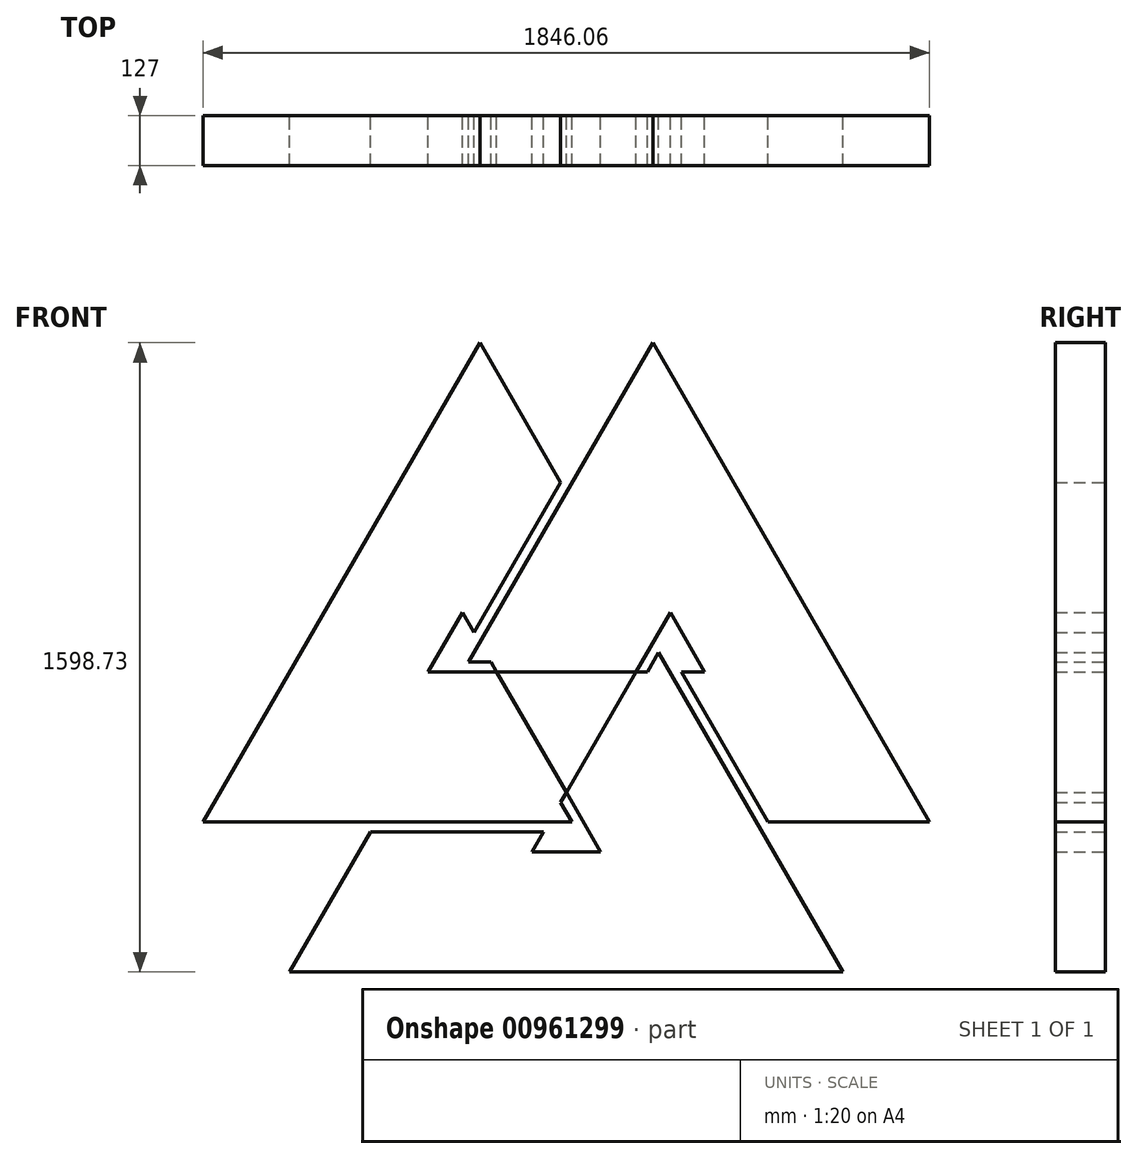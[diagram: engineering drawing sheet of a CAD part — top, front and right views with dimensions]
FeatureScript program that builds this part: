
annotation { "Feature Type Name" : "Feature", "Feature Type Description" : "" }
export const myFeature = defineFeature(function(context is Context, id is Id, definition is map)
    precondition{}
    {
        {
            var Q0;
            Q0=qCreatedBy(makeId("Front.planeOp"),FACE);
            var sketch = newSketch(context, id + "F0", { "sketchPlane" : qUnion([Q0])});
            skLineSegment(sketch, "E0", {"start": v(0, 0) * mm, "end": v(2286, 0) * mm});
            skLineSegment(sketch, "E1", {"start": v(2286, 0) * mm, "end": v(1143, 1979.73) * mm});
            skLineSegment(sketch, "E2", {"start": v(1143, 1979.73) * mm, "end": v(0, 0) * mm});
            skLineSegment(sketch, "E3", {"start": v(2346.83, 304.8) * mm, "end": v(-509.39, 304.8) * mm});
            skLineSegment(sketch, "E4", {"start": v(-334.16, 355.6) * mm, "end": v(2298.64, 355.6) * mm});
            skLineSegment(sketch, "E5", {"start": v(2223.65, 381) * mm, "end": v(-198.36, 381) * mm});
            skLineSegment(sketch, "E6", {"start": v(-45.03, 762) * mm, "end": v(2119.03, 762) * mm});
            skLineSegment(sketch, "E7", {"start": v(1921.9, 787.4) * mm, "end": v(200.29, 787.4) * mm});
            skLineSegment(sketch, "E8", {"start": v(2071.19, -237.53) * mm, "end": v(818.25, 1932.62) * mm});
            skLineSegment(sketch, "E9", {"start": v(806.35, 1851.63) * mm, "end": v(1965.85, -156.68) * mm});
            skLineSegment(sketch, "E10", {"start": v(1881.83, -61.95) * mm, "end": v(724.51, 1942.57) * mm});
            skLineSegment(sketch, "E11", {"start": v(1430.6, 1868.27) * mm, "end": v(168.06, -318.51) * mm});
            skLineSegment(sketch, "E12", {"start": v(281.56, -223.53) * mm, "end": v(1464.91, 1826.1) * mm});
            skLineSegment(sketch, "E13", {"start": v(1447.2, 1744.6) * mm, "end": v(340.04, -173.03) * mm});
            skLineSegment(sketch, "E14", {"start": v(1524.57, -255.97) * mm, "end": v(417.23, 1662) * mm});
            skLineSegment(sketch, "E15", {"start": v(472.91, 1616.36) * mm, "end": v(1604.16, -343.02) * mm});
            skLineSegment(sketch, "E16", {"start": v(715, -285.6) * mm, "end": v(1720.82, 1456.54) * mm});
            skLineSegment(sketch, "E17", {"start": v(1650.04, 1283.16) * mm, "end": v(696.9, -367.74) * mm});
            skSolve(sketch);
        }
        {
            var Q0;
            {var subQ0=sQuery(id+"F0.wireOp",EDGE,"E13");var subQ1=sQuery(id+"F0.wireOp",EDGE,"E0");var subQ2=makeQuery(id+"F0.imprint","INTERSECT",VERTEX,{"derivedFrom":[subQ1,subQ0]});Q0=makeQuery(id+"F0.imprint","IMPRINT",FACE,{"disambiguationData":[TD([[makeQuery(id+"F0.imprint","IMPRINT",EDGE,{"disambiguationData":[TD([[subQ2,-1.0]])],"derivedFrom":subQ1}),1.0]])]});}
            var Q1;
            {var subQ0=sQuery(id+"F0.wireOp",EDGE,"E16");var subQ1=sQuery(id+"F0.wireOp",EDGE,"E3");var subQ2=makeQuery(id+"F0.imprint","INTERSECT",VERTEX,{"derivedFrom":[subQ1,subQ0]});Q1=makeQuery(id+"F0.imprint","IMPRINT",FACE,{"disambiguationData":[TD([[makeQuery(id+"F0.imprint","IMPRINT",EDGE,{"disambiguationData":[TD([[subQ2,-1.0]])],"derivedFrom":subQ1}),-1.0]])]});}
            var Q2;
            {var subQ0=sQuery(id+"F0.wireOp",EDGE,"E16");var subQ1=sQuery(id+"F0.wireOp",EDGE,"E0");var subQ2=makeQuery(id+"F0.imprint","INTERSECT",VERTEX,{"derivedFrom":[subQ1,subQ0]});Q2=makeQuery(id+"F0.imprint","IMPRINT",FACE,{"disambiguationData":[TD([[makeQuery(id+"F0.imprint","IMPRINT",EDGE,{"disambiguationData":[TD([[subQ2,-1.0]])],"derivedFrom":subQ1}),1.0]])]});}
            var Q3;
            {var subQ0=sQuery(id+"F0.wireOp",EDGE,"E14");var subQ1=sQuery(id+"F0.wireOp",EDGE,"E0");var subQ2=makeQuery(id+"F0.imprint","INTERSECT",VERTEX,{"derivedFrom":[subQ1,subQ0]});Q3=makeQuery(id+"F0.imprint","IMPRINT",FACE,{"disambiguationData":[TD([[makeQuery(id+"F0.imprint","IMPRINT",EDGE,{"disambiguationData":[TD([[subQ2,-1.0]])],"derivedFrom":subQ1}),1.0]])]});}
            var Q4;
            {var subQ0=sQuery(id+"F0.wireOp",EDGE,"E17");var subQ1=sQuery(id+"F0.wireOp",EDGE,"E0");var subQ2=makeQuery(id+"F0.imprint","INTERSECT",VERTEX,{"derivedFrom":[subQ1,subQ0]});Q4=makeQuery(id+"F0.imprint","IMPRINT",FACE,{"disambiguationData":[TD([[makeQuery(id+"F0.imprint","IMPRINT",EDGE,{"disambiguationData":[TD([[subQ2,-1.0]])],"derivedFrom":subQ1}),1.0]])]});}
            var Q5;
            {var subQ0=sQuery(id+"F0.wireOp",EDGE,"E15");var subQ1=sQuery(id+"F0.wireOp",EDGE,"E0");var subQ2=makeQuery(id+"F0.imprint","INTERSECT",VERTEX,{"derivedFrom":[subQ1,subQ0]});Q5=makeQuery(id+"F0.imprint","IMPRINT",FACE,{"disambiguationData":[TD([[makeQuery(id+"F0.imprint","IMPRINT",EDGE,{"disambiguationData":[TD([[subQ2,-1.0]])],"derivedFrom":subQ1}),1.0]])]});}
            var Q6;
            {var subQ0=sQuery(id+"F0.wireOp",EDGE,"E10");var subQ1=sQuery(id+"F0.wireOp",EDGE,"E3");var subQ2=makeQuery(id+"F0.imprint","INTERSECT",VERTEX,{"derivedFrom":[subQ1,subQ0]});Q6=makeQuery(id+"F0.imprint","IMPRINT",FACE,{"disambiguationData":[TD([[makeQuery(id+"F0.imprint","IMPRINT",EDGE,{"disambiguationData":[TD([[subQ2,-1.0]])],"derivedFrom":subQ1}),-1.0]])]});}
            var Q7;
            {var subQ0=sQuery(id+"F0.wireOp",EDGE,"E15");var subQ1=sQuery(id+"F0.wireOp",EDGE,"E4");var subQ2=makeQuery(id+"F0.imprint","INTERSECT",VERTEX,{"derivedFrom":[subQ1,subQ0]});Q7=makeQuery(id+"F0.imprint","IMPRINT",FACE,{"disambiguationData":[TD([[makeQuery(id+"F0.imprint","IMPRINT",EDGE,{"disambiguationData":[TD([[subQ2,-1.0]])],"derivedFrom":subQ1}),1.0]])]});}
            var Q8;
            {var subQ1=sQuery(id+"F0.wireOp",EDGE,"E5");var subQ7=sQuery(id+"F0.wireOp",EDGE,"E10");var subQ9=makeQuery(id+"F0.imprint","INTERSECT",VERTEX,{"derivedFrom":[subQ1,subQ7]});Q8=makeQuery(id+"F0.imprint","IMPRINT",FACE,{"disambiguationData":[TD([[makeQuery(id+"F0.imprint","IMPRINT",EDGE,{"disambiguationData":[TD([[subQ9,-1.0]])],"derivedFrom":subQ1}),-1.0]])]});}
            var Q9;
            {var subQ0=sQuery(id+"F0.wireOp",EDGE,"E17");var subQ1=sQuery(id+"F0.wireOp",EDGE,"E6");var subQ2=makeQuery(id+"F0.imprint","INTERSECT",VERTEX,{"derivedFrom":[subQ1,subQ0]});Q9=makeQuery(id+"F0.imprint","IMPRINT",FACE,{"disambiguationData":[TD([[makeQuery(id+"F0.imprint","IMPRINT",EDGE,{"disambiguationData":[TD([[subQ2,-1.0]])],"derivedFrom":subQ1}),1.0]])]});}
            var Q10;
            {var subQ0=sQuery(id+"F0.wireOp",EDGE,"E10");var subQ1=sQuery(id+"F0.wireOp",EDGE,"E7");var subQ2=makeQuery(id+"F0.imprint","INTERSECT",VERTEX,{"derivedFrom":[subQ1,subQ0]});Q10=makeQuery(id+"F0.imprint","IMPRINT",FACE,{"disambiguationData":[TD([[makeQuery(id+"F0.imprint","IMPRINT",EDGE,{"disambiguationData":[TD([[subQ2,-1.0]])],"derivedFrom":subQ1}),-1.0]])]});}
            var Q11;
            {var subQ0=sQuery(id+"F0.wireOp",EDGE,"E5");var subQ1=sQuery(id+"F0.wireOp",EDGE,"E1");var subQ2=makeQuery(id+"F0.imprint","INTERSECT",VERTEX,{"derivedFrom":[subQ1,subQ0]});Q11=makeQuery(id+"F0.imprint","IMPRINT",FACE,{"disambiguationData":[TD([[makeQuery(id+"F0.imprint","IMPRINT",EDGE,{"disambiguationData":[TD([[subQ2,-1.0]])],"derivedFrom":subQ1}),1.0]])]});}
            var Q12;
            {var subQ0=sQuery(id+"F0.wireOp",EDGE,"E8");var subQ1=sQuery(id+"F0.wireOp",EDGE,"E5");var subQ2=makeQuery(id+"F0.imprint","INTERSECT",VERTEX,{"derivedFrom":[subQ1,subQ0]});Q12=makeQuery(id+"F0.imprint","IMPRINT",FACE,{"disambiguationData":[TD([[makeQuery(id+"F0.imprint","IMPRINT",EDGE,{"disambiguationData":[TD([[subQ2,-1.0]])],"derivedFrom":subQ1}),-1.0]])]});}
            var Q13;
            {var subQ0=sQuery(id+"F0.wireOp",EDGE,"E6");var subQ1=sQuery(id+"F0.wireOp",EDGE,"E1");var subQ2=makeQuery(id+"F0.imprint","INTERSECT",VERTEX,{"derivedFrom":[subQ1,subQ0]});Q13=makeQuery(id+"F0.imprint","IMPRINT",FACE,{"disambiguationData":[TD([[makeQuery(id+"F0.imprint","IMPRINT",EDGE,{"disambiguationData":[TD([[subQ2,-1.0]])],"derivedFrom":subQ1}),1.0]])]});}
            var Q14;
            {var subQ0=sQuery(id+"F0.wireOp",EDGE,"E7");var subQ1=sQuery(id+"F0.wireOp",EDGE,"E1");var subQ2=makeQuery(id+"F0.imprint","INTERSECT",VERTEX,{"derivedFrom":[subQ1,subQ0]});Q14=makeQuery(id+"F0.imprint","IMPRINT",FACE,{"disambiguationData":[TD([[makeQuery(id+"F0.imprint","IMPRINT",EDGE,{"disambiguationData":[TD([[subQ2,-1.0]])],"derivedFrom":subQ1}),1.0]])]});}
            var Q15;
            {var subQ0=sQuery(id+"F0.wireOp",EDGE,"E17");var subQ1=sQuery(id+"F0.wireOp",EDGE,"E1");var subQ2=makeQuery(id+"F0.imprint","INTERSECT",VERTEX,{"derivedFrom":[subQ1,subQ0]});Q15=makeQuery(id+"F0.imprint","IMPRINT",FACE,{"disambiguationData":[TD([[makeQuery(id+"F0.imprint","IMPRINT",EDGE,{"disambiguationData":[TD([[subQ2,-1.0]])],"derivedFrom":subQ1}),1.0]])]});}
            var Q16;
            {var subQ0=sQuery(id+"F0.wireOp",EDGE,"E16");var subQ1=sQuery(id+"F0.wireOp",EDGE,"E1");var subQ2=makeQuery(id+"F0.imprint","INTERSECT",VERTEX,{"derivedFrom":[subQ1,subQ0]});Q16=makeQuery(id+"F0.imprint","IMPRINT",FACE,{"disambiguationData":[TD([[makeQuery(id+"F0.imprint","IMPRINT",EDGE,{"disambiguationData":[TD([[subQ2,-1.0]])],"derivedFrom":subQ1}),1.0]])]});}
            var Q17;
            {var subQ0=sQuery(id+"F0.wireOp",EDGE,"E16");var subQ1=sQuery(id+"F0.wireOp",EDGE,"E8");var subQ2=makeQuery(id+"F0.imprint","INTERSECT",VERTEX,{"derivedFrom":[subQ1,subQ0]});Q17=makeQuery(id+"F0.imprint","IMPRINT",FACE,{"disambiguationData":[TD([[makeQuery(id+"F0.imprint","IMPRINT",EDGE,{"disambiguationData":[TD([[subQ2,-1.0]])],"derivedFrom":subQ1}),1.0]])]});}
            var Q18;
            {var subQ0=sQuery(id+"F0.wireOp",EDGE,"E13");var subQ1=sQuery(id+"F0.wireOp",EDGE,"E9");var subQ2=makeQuery(id+"F0.imprint","INTERSECT",VERTEX,{"derivedFrom":[subQ1,subQ0]});Q18=makeQuery(id+"F0.imprint","IMPRINT",FACE,{"disambiguationData":[TD([[makeQuery(id+"F0.imprint","IMPRINT",EDGE,{"disambiguationData":[TD([[subQ2,-1.0]])],"derivedFrom":subQ1}),-1.0]])]});}
            var Q19;
            {var subQ1=sQuery(id+"F0.wireOp",EDGE,"E7");var subQ7=sQuery(id+"F0.wireOp",EDGE,"E16");var subQ9=makeQuery(id+"F0.imprint","INTERSECT",VERTEX,{"derivedFrom":[subQ1,subQ7]});Q19=makeQuery(id+"F0.imprint","IMPRINT",FACE,{"disambiguationData":[TD([[makeQuery(id+"F0.imprint","IMPRINT",EDGE,{"disambiguationData":[TD([[subQ9,-1.0]])],"derivedFrom":subQ1}),-1.0]])]});}
            var Q20;
            {var subQ0=sQuery(id+"F0.wireOp",EDGE,"E15");var subQ1=sQuery(id+"F0.wireOp",EDGE,"E7");var subQ2=makeQuery(id+"F0.imprint","INTERSECT",VERTEX,{"derivedFrom":[subQ1,subQ0]});Q20=makeQuery(id+"F0.imprint","IMPRINT",FACE,{"disambiguationData":[TD([[makeQuery(id+"F0.imprint","IMPRINT",EDGE,{"disambiguationData":[TD([[subQ2,-1.0]])],"derivedFrom":subQ1}),-1.0]])]});}
            var Q21;
            {var subQ0=sQuery(id+"F0.wireOp",EDGE,"E14");var subQ1=sQuery(id+"F0.wireOp",EDGE,"E7");var subQ2=makeQuery(id+"F0.imprint","INTERSECT",VERTEX,{"derivedFrom":[subQ1,subQ0]});Q21=makeQuery(id+"F0.imprint","IMPRINT",FACE,{"disambiguationData":[TD([[makeQuery(id+"F0.imprint","IMPRINT",EDGE,{"disambiguationData":[TD([[subQ2,-1.0]])],"derivedFrom":subQ1}),-1.0]])]});}
            var Q22;
            {var subQ1=sQuery(id+"F0.wireOp",EDGE,"E5");var subQ5=sQuery(id+"F0.wireOp",EDGE,"E16");var subQ6=makeQuery(id+"F0.imprint","INTERSECT",VERTEX,{"derivedFrom":[subQ1,subQ5]});Q22=makeQuery(id+"F0.imprint","IMPRINT",FACE,{"disambiguationData":[TD([[makeQuery(id+"F0.imprint","IMPRINT",EDGE,{"disambiguationData":[TD([[subQ6,-1.0]])],"derivedFrom":subQ1}),-1.0]])]});}
            var Q23;
            {var subQ0=sQuery(id+"F0.wireOp",EDGE,"E13");var subQ1=sQuery(id+"F0.wireOp",EDGE,"E5");var subQ2=makeQuery(id+"F0.imprint","INTERSECT",VERTEX,{"derivedFrom":[subQ1,subQ0]});Q23=makeQuery(id+"F0.imprint","IMPRINT",FACE,{"disambiguationData":[TD([[makeQuery(id+"F0.imprint","IMPRINT",EDGE,{"disambiguationData":[TD([[subQ2,-1.0]])],"derivedFrom":subQ1}),-1.0]])]});}
            var Q24;
            {var subQ0=sQuery(id+"F0.wireOp",EDGE,"E12");var subQ1=sQuery(id+"F0.wireOp",EDGE,"E5");var subQ2=makeQuery(id+"F0.imprint","INTERSECT",VERTEX,{"derivedFrom":[subQ1,subQ0]});Q24=makeQuery(id+"F0.imprint","IMPRINT",FACE,{"disambiguationData":[TD([[makeQuery(id+"F0.imprint","IMPRINT",EDGE,{"disambiguationData":[TD([[subQ2,-1.0]])],"derivedFrom":subQ1}),-1.0]])]});}
            var Q25;
            {var subQ0=sQuery(id+"F0.wireOp",EDGE,"E6");var subQ1=sQuery(id+"F0.wireOp",EDGE,"E2");var subQ2=makeQuery(id+"F0.imprint","INTERSECT",VERTEX,{"derivedFrom":[subQ1,subQ0]});Q25=makeQuery(id+"F0.imprint","IMPRINT",FACE,{"disambiguationData":[TD([[makeQuery(id+"F0.imprint","IMPRINT",EDGE,{"disambiguationData":[TD([[subQ2,-1.0]])],"derivedFrom":subQ1}),1.0]])]});}
            var Q26;
            {var subQ0=sQuery(id+"F0.wireOp",EDGE,"E7");var subQ1=sQuery(id+"F0.wireOp",EDGE,"E2");var subQ2=makeQuery(id+"F0.imprint","INTERSECT",VERTEX,{"derivedFrom":[subQ1,subQ0]});Q26=makeQuery(id+"F0.imprint","IMPRINT",FACE,{"disambiguationData":[TD([[makeQuery(id+"F0.imprint","IMPRINT",EDGE,{"disambiguationData":[TD([[subQ2,-1.0]])],"derivedFrom":subQ1}),1.0]])]});}
            var Q27;
            {var subQ0=sQuery(id+"F0.wireOp",EDGE,"E14");var subQ1=sQuery(id+"F0.wireOp",EDGE,"E2");var subQ2=makeQuery(id+"F0.imprint","INTERSECT",VERTEX,{"derivedFrom":[subQ1,subQ0]});Q27=makeQuery(id+"F0.imprint","IMPRINT",FACE,{"disambiguationData":[TD([[makeQuery(id+"F0.imprint","IMPRINT",EDGE,{"disambiguationData":[TD([[subQ2,-1.0]])],"derivedFrom":subQ1}),1.0]])]});}
            var Q28;
            {var subQ0=sQuery(id+"F0.wireOp",EDGE,"E15");var subQ1=sQuery(id+"F0.wireOp",EDGE,"E2");var subQ2=makeQuery(id+"F0.imprint","INTERSECT",VERTEX,{"derivedFrom":[subQ1,subQ0]});Q28=makeQuery(id+"F0.imprint","IMPRINT",FACE,{"disambiguationData":[TD([[makeQuery(id+"F0.imprint","IMPRINT",EDGE,{"disambiguationData":[TD([[subQ2,-1.0]])],"derivedFrom":subQ1}),1.0]])]});}
            var Q29;
            {var subQ0=sQuery(id+"F0.wireOp",EDGE,"E10");var subQ1=sQuery(id+"F0.wireOp",EDGE,"E2");var subQ2=makeQuery(id+"F0.imprint","INTERSECT",VERTEX,{"derivedFrom":[subQ1,subQ0]});Q29=makeQuery(id+"F0.imprint","IMPRINT",FACE,{"disambiguationData":[TD([[makeQuery(id+"F0.imprint","IMPRINT",EDGE,{"disambiguationData":[TD([[subQ2,-1.0]])],"derivedFrom":subQ1}),1.0]])]});}
            var Q30;
            {var subQ0=sQuery(id+"F0.wireOp",EDGE,"E12");var subQ1=sQuery(id+"F0.wireOp",EDGE,"E10");var subQ2=makeQuery(id+"F0.imprint","INTERSECT",VERTEX,{"derivedFrom":[subQ1,subQ0]});Q30=makeQuery(id+"F0.imprint","IMPRINT",FACE,{"disambiguationData":[TD([[makeQuery(id+"F0.imprint","IMPRINT",EDGE,{"disambiguationData":[TD([[subQ2,-1.0]])],"derivedFrom":subQ1}),1.0]])]});}
            var Q31;
            {var subQ0=sQuery(id+"F0.wireOp",EDGE,"E17");var subQ1=sQuery(id+"F0.wireOp",EDGE,"E5");var subQ2=makeQuery(id+"F0.imprint","INTERSECT",VERTEX,{"derivedFrom":[subQ1,subQ0]});Q31=makeQuery(id+"F0.imprint","IMPRINT",FACE,{"disambiguationData":[TD([[makeQuery(id+"F0.imprint","IMPRINT",EDGE,{"disambiguationData":[TD([[subQ2,-1.0]])],"derivedFrom":subQ1}),-1.0]])]});}
            var Q32;
            {var subQ0=sQuery(id+"F0.wireOp",EDGE,"E14");var subQ1=sQuery(id+"F0.wireOp",EDGE,"E5");var subQ2=makeQuery(id+"F0.imprint","INTERSECT",VERTEX,{"derivedFrom":[subQ1,subQ0]});Q32=makeQuery(id+"F0.imprint","IMPRINT",FACE,{"disambiguationData":[TD([[makeQuery(id+"F0.imprint","IMPRINT",EDGE,{"disambiguationData":[TD([[subQ2,-1.0]])],"derivedFrom":subQ1}),-1.0]])]});}
            var Q33;
            {var subQ0=sQuery(id+"F0.wireOp",EDGE,"E16");var subQ1=sQuery(id+"F0.wireOp",EDGE,"E6");var subQ2=makeQuery(id+"F0.imprint","INTERSECT",VERTEX,{"derivedFrom":[subQ1,subQ0]});Q33=makeQuery(id+"F0.imprint","IMPRINT",FACE,{"disambiguationData":[TD([[makeQuery(id+"F0.imprint","IMPRINT",EDGE,{"disambiguationData":[TD([[subQ2,-1.0]])],"derivedFrom":subQ1}),-1.0]])]});}
            var Q34;
            {var subQ0=sQuery(id+"F0.wireOp",EDGE,"E14");var subQ1=sQuery(id+"F0.wireOp",EDGE,"E6");var subQ2=makeQuery(id+"F0.imprint","INTERSECT",VERTEX,{"derivedFrom":[subQ1,subQ0]});Q34=makeQuery(id+"F0.imprint","IMPRINT",FACE,{"disambiguationData":[TD([[makeQuery(id+"F0.imprint","IMPRINT",EDGE,{"disambiguationData":[TD([[subQ2,-1.0]])],"derivedFrom":subQ1}),-1.0]])]});}
            var Q35;
            {var subQ0=sQuery(id+"F0.wireOp",EDGE,"E15");var subQ1=sQuery(id+"F0.wireOp",EDGE,"E6");var subQ2=makeQuery(id+"F0.imprint","INTERSECT",VERTEX,{"derivedFrom":[subQ1,subQ0]});Q35=makeQuery(id+"F0.imprint","IMPRINT",FACE,{"disambiguationData":[TD([[makeQuery(id+"F0.imprint","IMPRINT",EDGE,{"disambiguationData":[TD([[subQ2,-1.0]])],"derivedFrom":subQ1}),1.0]])]});}
            extrude(context, id + "F1", {"entities" : qUnion([Q0, Q1, Q2, Q3, Q4, Q5, Q6, Q7, Q8, Q9, Q10, Q11, Q12, Q13, Q14, Q15, Q16, Q17, Q18, Q19, Q20, Q21, Q22, Q23, Q24, Q25, Q26, Q27, Q28, Q29, Q30, Q31, Q32, Q33, Q34, Q35]), "depth" : 127 * mm, "offsetDistance" : 25.4 * mm});
        }
    });
